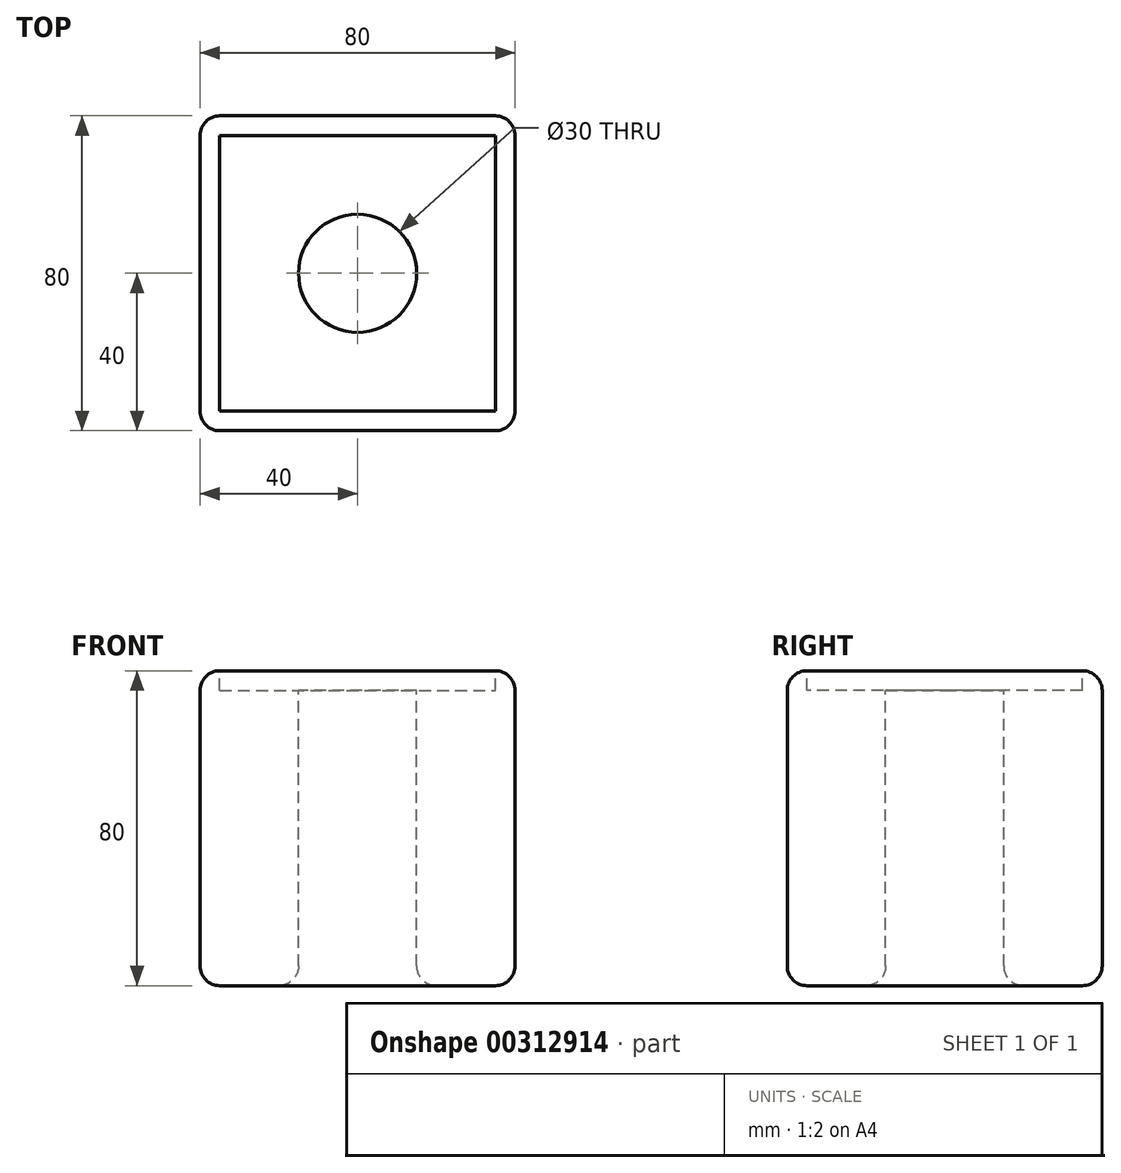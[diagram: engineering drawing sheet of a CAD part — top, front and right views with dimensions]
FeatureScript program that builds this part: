
annotation { "Feature Type Name" : "Feature", "Feature Type Description" : "" }
export const myFeature = defineFeature(function(context is Context, id is Id, definition is map)
    precondition{}
    {
        {
            var Q0;
            Q0=qCreatedBy(makeId("Top.planeOp"),FACE);
            var sketch = newSketch(context, id + "F0", { "sketchPlane" : qUnion([Q0])});
            skLineSegment(sketch, "E0.bottom", {"start": v(-40, 40) * mm, "end": v(40, 40) * mm});
            skLineSegment(sketch, "E0.top", {"start": v(-40, -40) * mm, "end": v(40, -40) * mm});
            skLineSegment(sketch, "E0.left", {"start": v(-40, 40) * mm, "end": v(-40, -40) * mm});
            skLineSegment(sketch, "E0.right", {"start": v(40, 40) * mm, "end": v(40, -40) * mm});
            skPoint(sketch, "E0.middle", {"position": v(0, 0) * mm});
            skSolve(sketch);
        }
        {
            var Q0;
            Q0 = qSketchRegion(id + "F0", true);
            extrude(context, id + "F1", {"entities" : qUnion([Q0]), "endBound" : BoundingType.SYMMETRIC, "depth" : 80 * mm});
        }
        {
            var Q0;
            Q0=makeQuery(id+"F1.opExtrude","CAP_FACE",FACE,{"disambiguationData":[OSD([sQuery(id+"F0.wireOp",EDGE,"E0.bottom"),sQuery(id+"F0.wireOp",EDGE,"E0.top"),sQuery(id+"F0.wireOp",EDGE,"E0.left"),sQuery(id+"F0.wireOp",EDGE,"E0.right")])],"isStart":false});
            var Q1;
            Q1=makeQuery(id+"F1.opExtrude","SWEPT_EDGE",EDGE,{"disambiguationData":[OSD([sQuery(id+"F0.wireOp",EDGE,"E0.bottom"),sQuery(id+"F0.wireOp",EDGE,"E0.left")])]});
            var Q2;
            Q2=makeQuery(id+"F1.opExtrude","CAP_EDGE",EDGE,{"disambiguationData":[OSD([sQuery(id+"F0.wireOp",EDGE,"E0.left")])],"isStart":false});
            var Q3;
            Q3=makeQuery(id+"F1.opExtrude","CAP_EDGE",EDGE,{"disambiguationData":[OSD([sQuery(id+"F0.wireOp",EDGE,"E0.right")])],"isStart":false});
            var Q4;
            Q4=makeQuery(id+"F1.opExtrude","CAP_EDGE",EDGE,{"disambiguationData":[OSD([sQuery(id+"F0.wireOp",EDGE,"E0.bottom")])],"isStart":true});
            var Q5;
            Q5=makeQuery(id+"F1.opExtrude","CAP_EDGE",EDGE,{"disambiguationData":[OSD([sQuery(id+"F0.wireOp",EDGE,"E0.left")])],"isStart":true});
            var Q6;
            Q6=makeQuery(id+"F1.opExtrude","SWEPT_EDGE",EDGE,{"disambiguationData":[OSD([sQuery(id+"F0.wireOp",EDGE,"E0.top"),sQuery(id+"F0.wireOp",EDGE,"E0.left")])]});
            var Q7;
            Q7=makeQuery(id+"F1.opExtrude","SWEPT_EDGE",EDGE,{"disambiguationData":[OSD([sQuery(id+"F0.wireOp",EDGE,"E0.top"),sQuery(id+"F0.wireOp",EDGE,"E0.right")])]});
            var Q8;
            Q8=makeQuery(id+"F1.opExtrude","CAP_EDGE",EDGE,{"disambiguationData":[OSD([sQuery(id+"F0.wireOp",EDGE,"E0.right")])],"isStart":true});
            var Q9;
            Q9=makeQuery(id+"F1.opExtrude","SWEPT_EDGE",EDGE,{"disambiguationData":[OSD([sQuery(id+"F0.wireOp",EDGE,"E0.bottom"),sQuery(id+"F0.wireOp",EDGE,"E0.right")])]});
            var Q10;
            Q10=makeQuery(id+"F1.opExtrude","CAP_EDGE",EDGE,{"disambiguationData":[OSD([sQuery(id+"F0.wireOp",EDGE,"E0.top")])],"isStart":true});
            fillet(context, id + "F2", {"entities" : qUnion([Q0, Q1, Q2, Q3, Q4, Q5, Q6, Q7, Q8, Q9, Q10]), "radius" : 5 * mm, "tangentPropagation" : true, "allowEdgeOverflow" : false});
        }
        {
            var Q0;
            Q0=makeQuery(id+"F1.opExtrude","CAP_FACE",FACE,{"disambiguationData":[OSD([sQuery(id+"F0.wireOp",EDGE,"E0.bottom"),sQuery(id+"F0.wireOp",EDGE,"E0.top"),sQuery(id+"F0.wireOp",EDGE,"E0.left"),sQuery(id+"F0.wireOp",EDGE,"E0.right")])],"isStart":false});
            var sketch = newSketch(context, id + "F3", { "sketchPlane" : qUnion([Q0])});
            skCircle(sketch, "E1", {"center": v(0, 0) * mm, "radius": 15 * mm});
            skSolve(sketch);
        }
        {
            var Q0;
            Q0=makeQuery(id+"F3.imprint","IMPRINT",FACE,{"disambiguationData":[TD([[makeQuery(id+"F3.imprint","IMPRINT",EDGE,{"derivedFrom":sQuery(id+"F3.wireOp",EDGE,"E1")}),1.0]])]});
            extrude(context, id + "F4", {"entities" : qUnion([Q0]), "operationType" : NewBodyOperationType.REMOVE, "endBound" : BoundingType.THROUGH_ALL, "oppositeDirection" : true, "depth" : 25 * mm});
        }
        {
            var Q0;
            Q0=makeQuery(id+"F4.boolean.opBoolean","INTERSECT",EDGE,{"derivedFrom":[makeQuery(id+"F1.opExtrude","CAP_FACE",FACE,{"disambiguationData":[OSD([sQuery(id+"F0.wireOp",EDGE,"E0.bottom"),sQuery(id+"F0.wireOp",EDGE,"E0.top"),sQuery(id+"F0.wireOp",EDGE,"E0.left"),sQuery(id+"F0.wireOp",EDGE,"E0.right")])],"isStart":true}),makeQuery(id+"F4.opExtrude","SWEPT_FACE",FACE,{"disambiguationData":[OSD([sQuery(id+"F3.wireOp",EDGE,"E1")])]})]});
            fillet(context, id + "F5", {"entities" : qUnion([Q0]), "radius" : 5 * mm, "tangentPropagation" : true, "allowEdgeOverflow" : false});
        }
        {
            var Q0;
            Q0=makeQuery(id+"F1.opExtrude","CAP_FACE",FACE,{"disambiguationData":[OSD([sQuery(id+"F0.wireOp",EDGE,"E0.bottom"),sQuery(id+"F0.wireOp",EDGE,"E0.top"),sQuery(id+"F0.wireOp",EDGE,"E0.left"),sQuery(id+"F0.wireOp",EDGE,"E0.right")])],"isStart":false});
            extrude(context, id + "F6", {"entities" : qUnion([Q0]), "operationType" : NewBodyOperationType.REMOVE, "oppositeDirection" : true, "depth" : 5 * mm});
        }
    });
